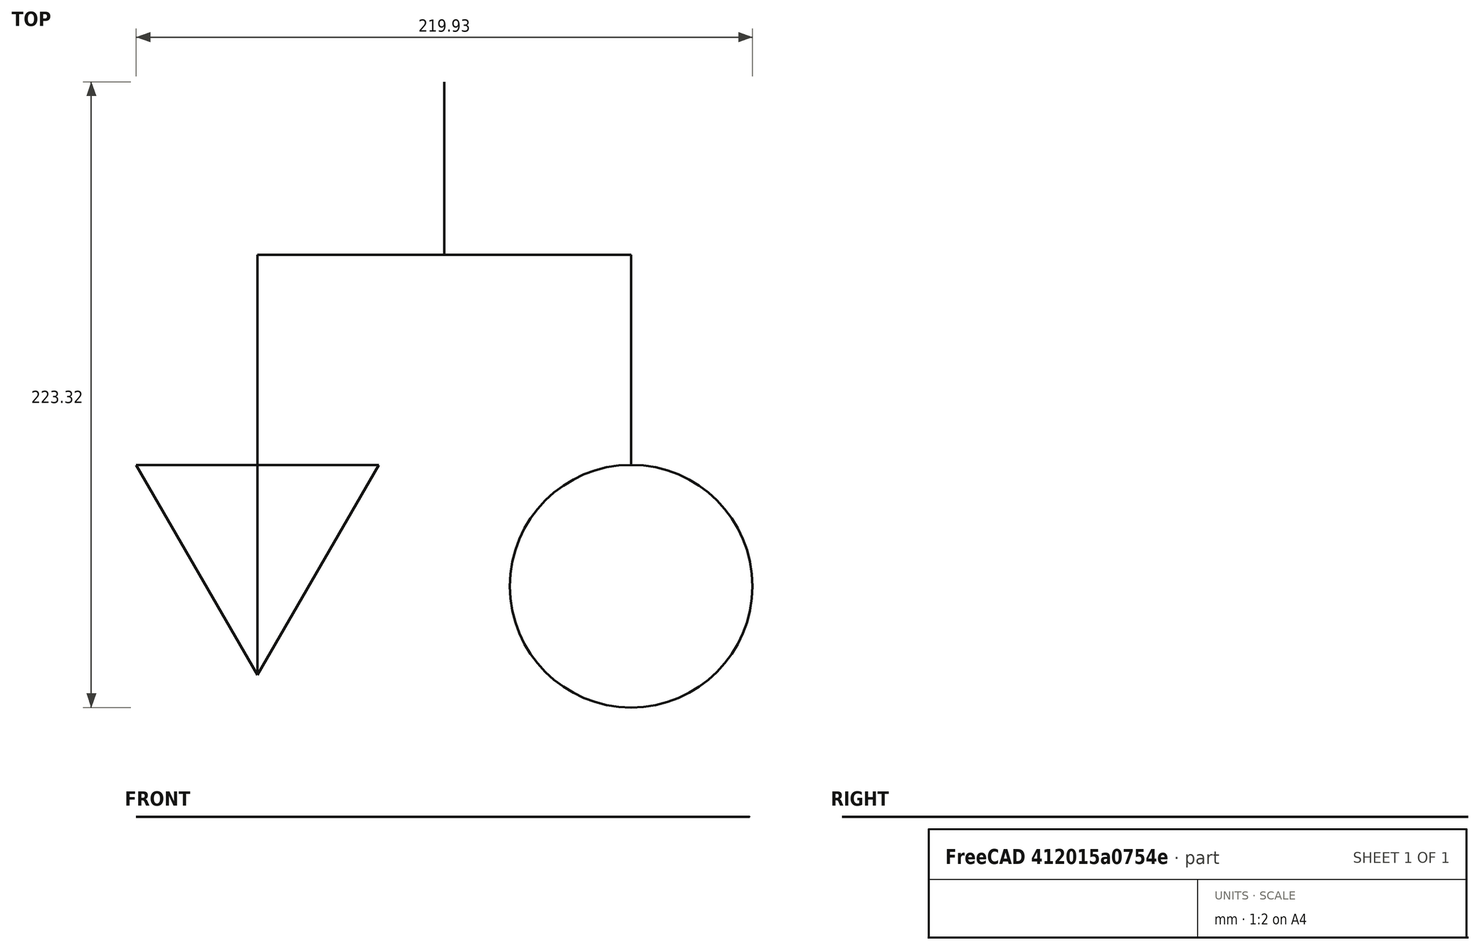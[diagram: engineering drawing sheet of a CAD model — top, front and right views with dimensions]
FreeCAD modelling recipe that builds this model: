
FCSTD DOCUMENT  (FreeCAD 1.1R20260325 (Git shallow))
Label: Interruptor_Tomada_Media_1modulo_110v_com_simbologia
License: All rights reserved
LicenseURL: http://en.wikipedia.org/wiki/All_rights_reserved
objects: Part::FeaturePython×1, Part::Feature×1, App::DocumentObjectGroup×1
note: 2 computed .brp shape members not serialized (recipe doc carries the construction recipe); baked Part::Feature solids carry a one-line shape summary decoded from their .brp

FEATURE [Part::FeaturePython] Component  label="Interruptor_Tomada_110v_media"  # Arch/BIM 0 (typed FeaturePython)
  HorizontalArea = 0
  IfcData = attributes={"GlobalId": {"name": "GlobalId", "type": "IfcGloballyUniqueId", "is_enum": false, "enum_values": []}, "Description": {"... (+538 chars omitted),+1 more (map truncated)
  IfcType = 0
  MoveBase = false
  MoveWithHost = false
  PerimeterLength = 0
  Placement = pos=(0,0,1200) rot=(0,0,1;0rad)
  PredefinedType = 0
  VerticalArea = 0
FEATURE [Part::Feature] Compound002002002004005002002003003002003005002002005002002002002002002002002002002002  label="Simbologia_Tomada_Interruptor"
  Placement = pos=(804.665,1993.94,1191.87) rot=(0,0,-1;1.5708rad)
  shape: bbox 219.9 x 223.3 x 2e-07 mm, 1 faces, 0 solids (baked)
FEATURE [App::DocumentObjectGroup] Group  label="Interruptor_Tomada_media"
  Group = -> [Component,Compound002002002004005002002003003002003005002002005002002002002002002002002002002002]
